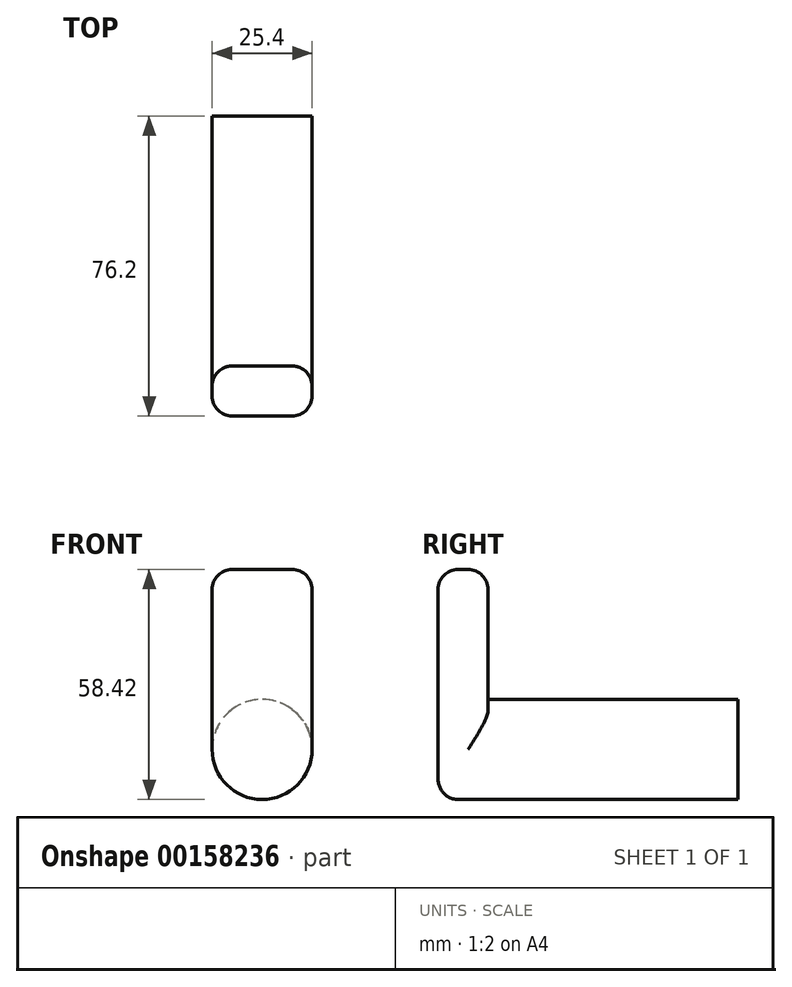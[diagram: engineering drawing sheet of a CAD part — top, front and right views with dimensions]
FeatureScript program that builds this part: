
annotation { "Feature Type Name" : "Feature", "Feature Type Description" : "" }
export const myFeature = defineFeature(function(context is Context, id is Id, definition is map)
    precondition{}
    {
        {
            var Q0;
            Q0=qCreatedBy(makeId("Front.planeOp"),FACE);
            var sketch = newSketch(context, id + "F0", { "sketchPlane" : qUnion([Q0])});
            skCircle(sketch, "E0", {"center": v(0, 0) * mm, "radius": 12.7 * mm});
            skSolve(sketch);
        }
        {
            var Q0;
            Q0=makeQuery(id+"F0.imprint","IMPRINT",FACE,{"disambiguationData":[TD([[makeQuery(id+"F0.imprint","IMPRINT",EDGE,{"derivedFrom":sQuery(id+"F0.wireOp",EDGE,"E0")}),1.0]])]});
            extrude(context, id + "F1", {"entities" : qUnion([Q0]), "endBound" : BoundingType.SYMMETRIC, "depth" : 50.8 * mm});
        }
        {
            var Q0;
            Q0=qCreatedBy(makeId("Top.planeOp"),FACE);
            var sketch = newSketch(context, id + "F2", { "sketchPlane" : qUnion([Q0])});
            skLineSegment(sketch, "E1.bottom", {"start": v(12.7, -25.4) * mm, "end": v(-12.7, -25.4) * mm});
            skLineSegment(sketch, "E1.left", {"start": v(12.7, -25.4) * mm, "end": v(12.7, -12.7) * mm});
            skLineSegment(sketch, "E1.right", {"start": v(-12.7, -25.4) * mm, "end": v(-12.7, -12.7) * mm});
            skLineSegment(sketch, "E2", {"start": v(-12.7, -12.7) * mm, "end": v(12.7, -12.7) * mm});
            skSolve(sketch);
        }
        {
            var Q0;
            Q0 = qSketchRegion(id + "F2", true);
            extrude(context, id + "F3", {"entities" : qUnion([Q0]), "operationType" : NewBodyOperationType.ADD, "depth" : 45.72 * mm});
        }
        {
            var Q0;
            Q0=makeQuery(id+"F3.opExtrude","CAP_EDGE",EDGE,{"disambiguationData":[OSD([sQuery(id+"F2.wireOp",EDGE,"E1.right")])],"isStart":false});
            var Q1;
            Q1=makeQuery(id+"F3.opExtrude","CAP_EDGE",EDGE,{"disambiguationData":[OSD([sQuery(id+"F2.wireOp",EDGE,"E1.left")])],"isStart":false});
            var Q2;
            Q2=makeQuery(id+"F1.opExtrude","CAP_EDGE",EDGE,{"disambiguationData":[OSD([sQuery(id+"F0.wireOp",EDGE,"E0")])],"isStart":false});
            var Q3;
            Q3=makeQuery(id+"F3.opExtrude","CAP_EDGE",EDGE,{"disambiguationData":[OSD([sQuery(id+"F2.wireOp",EDGE,"E1.bottom")])],"isStart":false});
            fillet(context, id + "F4", {"entities" : qUnion([Q0, Q1, Q2, Q3]), "radius" : 5.08 * mm, "tangentPropagation" : true, "allowEdgeOverflow" : false});
        }
        {
            var Q0;
            Q0=makeQuery(id+"F3.opExtrude","CAP_EDGE",EDGE,{"disambiguationData":[OSD([sQuery(id+"F2.wireOp",EDGE,"E2")])],"isStart":false});
            fillet(context, id + "F5", {"entities" : qUnion([Q0]), "radius" : 5.08 * mm, "tangentPropagation" : true, "allowEdgeOverflow" : false});
        }
        {
            var Q0;
            Q0=makeQuery(id+"F1.opExtrude","CAP_FACE",FACE,{"disambiguationData":[OSD([sQuery(id+"F0.wireOp",EDGE,"E0")])],"isStart":true});
            var sketch = newSketch(context, id + "F6", { "sketchPlane" : qUnion([Q0])});
            skCircle(sketch, "E3", {"center": v(0, 0) * mm, "radius": 12.7 * mm});
            skSolve(sketch);
        }
        {
            var Q0;
            Q0 = qSketchRegion(id + "F6", true);
            extrude(context, id + "F7", {"entities" : qUnion([Q0]), "operationType" : NewBodyOperationType.ADD, "depth" : 25.4 * mm});
        }
    });
